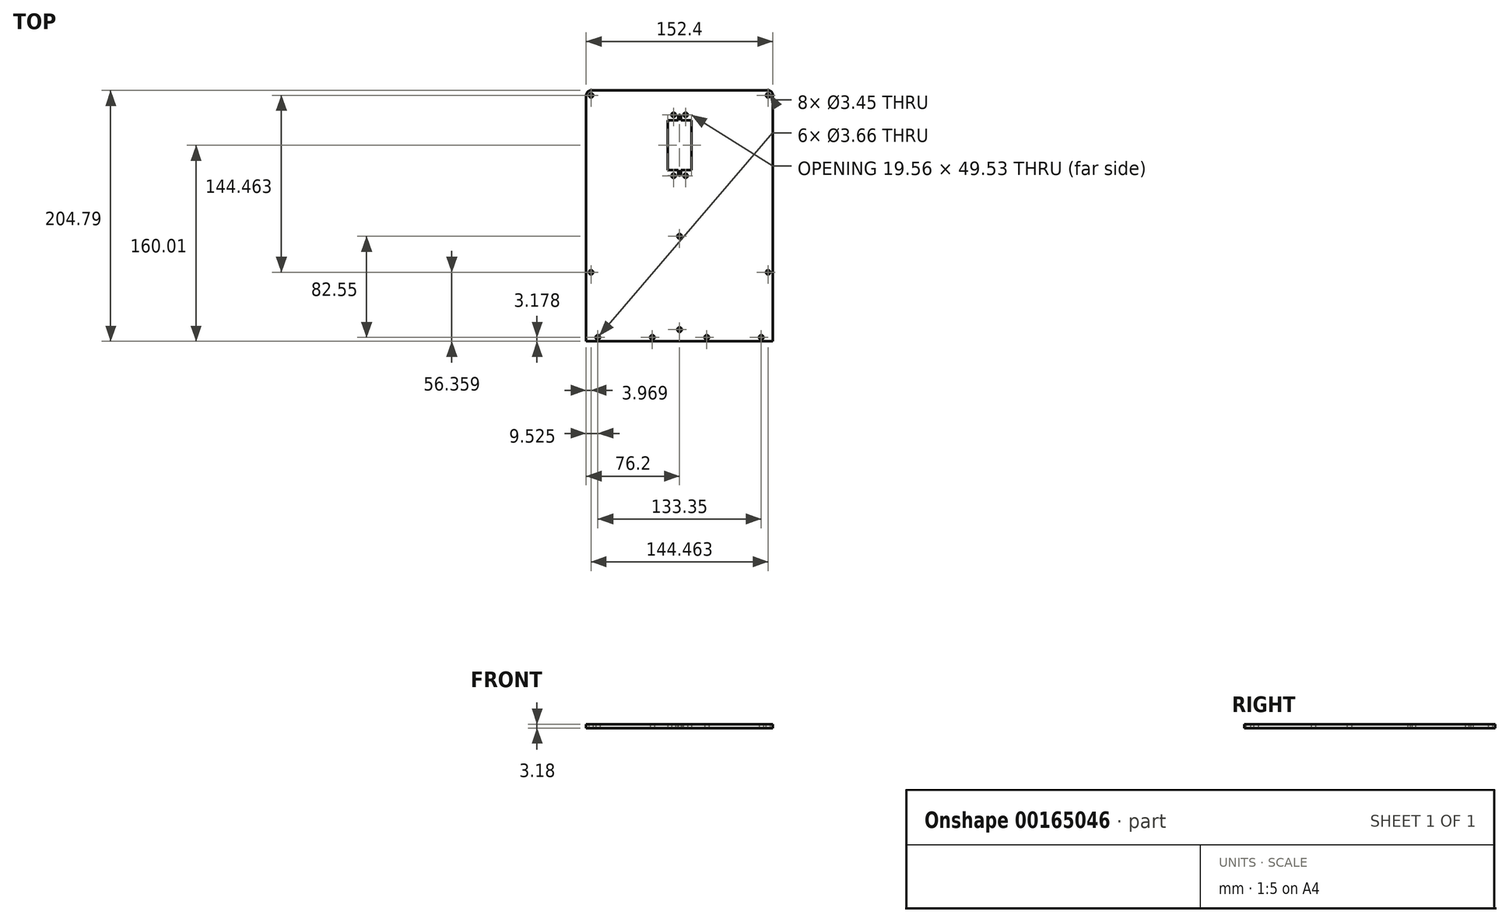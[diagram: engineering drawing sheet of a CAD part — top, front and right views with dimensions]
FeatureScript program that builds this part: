
annotation { "Feature Type Name" : "Feature", "Feature Type Description" : "" }
export const myFeature = defineFeature(function(context is Context, id is Id, definition is map)
    precondition{}
    {
        {
            var Q0;
            Q0=qCreatedBy(makeId("Top.planeOp"),FACE);
            var sketch = newSketch(context, id + "F0", { "sketchPlane" : qUnion([Q0])});
            skPoint(sketch, "E0.middle", {"position": v(0, 0) * mm});
            skLineSegment(sketch, "E1.bottom", {"start": v(-72.23, 72.23) * mm, "end": v(72.23, 72.23) * mm, "construction": true});
            skLineSegment(sketch, "E1.top", {"start": v(-72.23, -72.23) * mm, "end": v(72.23, -72.23) * mm, "construction": true});
            skLineSegment(sketch, "E1.left", {"start": v(-72.23, 72.23) * mm, "end": v(-72.23, -72.23) * mm, "construction": true});
            skLineSegment(sketch, "E1.right", {"start": v(72.23, 72.23) * mm, "end": v(72.23, -72.23) * mm, "construction": true});
            skCircle(sketch, "E2", {"center": v(-72.23, 72.23) * mm, "radius": 1.73 * mm});
            skCircle(sketch, "E3", {"center": v(72.23, 72.23) * mm, "radius": 1.73 * mm});
            skCircle(sketch, "E4", {"center": v(72.23, -72.23) * mm, "radius": 1.73 * mm});
            skCircle(sketch, "E5", {"center": v(-72.23, -72.23) * mm, "radius": 1.73 * mm});
            skLineSegment(sketch, "E6.bottom", {"start": v(76.2, -128.59) * mm, "end": v(-76.2, -128.59) * mm});
            skLineSegment(sketch, "E6.top", {"start": v(76.2, 76.2) * mm, "end": v(-76.2, 76.2) * mm});
            skLineSegment(sketch, "E6.left", {"start": v(76.2, -128.59) * mm, "end": v(76.2, 76.2) * mm});
            skLineSegment(sketch, "E6.right", {"start": v(-76.2, -128.59) * mm, "end": v(-76.2, 76.2) * mm});
            skLineSegment(sketch, "E7", {"start": v(0, 72.23) * mm, "end": v(0, 76.2) * mm, "construction": true});
            skLineSegment(sketch, "E8", {"start": v(-72.23, 72.23) * mm, "end": v(-76.2, 72.23) * mm, "construction": true});
            skLineSegment(sketch, "E9", {"start": v(66.68, -125.41) * mm, "end": v(76.2, -125.41) * mm, "construction": true});
            skCircle(sketch, "E10", {"center": v(-66.68, -125.41) * mm, "radius": 1.83 * mm});
            skCircle(sketch, "E11", {"center": v(22.23, -125.41) * mm, "radius": 1.83 * mm});
            skCircle(sketch, "E12", {"center": v(66.68, -125.41) * mm, "radius": 1.83 * mm});
            skLineSegment(sketch, "E13", {"start": v(22.23, -125.41) * mm, "end": v(66.68, -125.41) * mm, "construction": true});
            skLineSegment(sketch, "E14", {"start": v(22.23, -125.41) * mm, "end": v(-22.23, -125.41) * mm, "construction": true});
            skLineSegment(sketch, "E15", {"start": v(-22.23, -125.41) * mm, "end": v(-66.68, -125.41) * mm, "construction": true});
            skLineSegment(sketch, "E16", {"start": v(0, -125.41) * mm, "end": v(0, -128.59) * mm, "construction": true});
            skCircle(sketch, "E17", {"center": v(-22.23, -125.41) * mm, "radius": 1.83 * mm});
            skLineSegment(sketch, "E18", {"start": v(0, 0) * mm, "end": v(0, -42.86) * mm, "construction": true});
            skLineSegment(sketch, "E19", {"start": v(0, -42.86) * mm, "end": v(0, -119.06) * mm, "construction": true});
            skLineSegment(sketch, "E20", {"start": v(0, -119.06) * mm, "end": v(0, -125.41) * mm, "construction": true});
            skCircle(sketch, "E21", {"center": v(0, -42.86) * mm, "radius": 1.83 * mm});
            skCircle(sketch, "E22", {"center": v(0, -119.06) * mm, "radius": 1.83 * mm});
            skLineSegment(sketch, "E23", {"start": v(0, 0) * mm, "end": v(0, 31.42) * mm, "construction": true});
            skLineSegment(sketch, "E24.bottom", {"start": v(4.89, 6.53) * mm, "end": v(-4.89, 6.53) * mm, "construction": true});
            skLineSegment(sketch, "E24.top", {"start": v(4.89, 56.31) * mm, "end": v(-4.89, 56.31) * mm, "construction": true});
            skLineSegment(sketch, "E24.left", {"start": v(4.89, 6.53) * mm, "end": v(4.89, 56.31) * mm, "construction": true});
            skLineSegment(sketch, "E24.right", {"start": v(-4.89, 6.53) * mm, "end": v(-4.89, 56.31) * mm, "construction": true});
            skPoint(sketch, "E24.middle", {"position": v(0, 31.42) * mm});
            skCircle(sketch, "E25", {"center": v(4.89, 56.31) * mm, "radius": 3.97 * mm, "construction": true});
            skLineSegment(sketch, "E26", {"start": v(9.78, 31.42) * mm, "end": v(-9.78, 31.42) * mm, "construction": true});
            skLineSegment(sketch, "E27.bottom", {"start": v(1.02, 51.74) * mm, "end": v(9.78, 51.74) * mm});
            skLineSegment(sketch, "E27.top", {"start": v(1.02, 11.1) * mm, "end": v(9.78, 11.1) * mm});
            skLineSegment(sketch, "E27.right", {"start": v(9.78, 51.74) * mm, "end": v(9.78, 11.1) * mm});
            skLineSegment(sketch, "E28.bottom", {"start": v(-9.78, 51.74) * mm, "end": v(-1.02, 51.74) * mm});
            skLineSegment(sketch, "E28.top", {"start": v(-9.78, 11.1) * mm, "end": v(-1.02, 11.1) * mm});
            skLineSegment(sketch, "E28.left", {"start": v(-9.78, 51.74) * mm, "end": v(-9.78, 11.1) * mm});
            skLineSegment(sketch, "E29.bottom", {"start": v(1.02, 11.1) * mm, "end": v(-1.02, 11.1) * mm, "construction": true});
            skLineSegment(sketch, "E29.top", {"start": v(1.02, 7.67) * mm, "end": v(-1.02, 7.67) * mm, "construction": true});
            skLineSegment(sketch, "E29.left", {"start": v(1.02, 11.1) * mm, "end": v(1.02, 7.67) * mm});
            skLineSegment(sketch, "E29.right", {"start": v(-1.02, 11.1) * mm, "end": v(-1.02, 7.67) * mm});
            skLineSegment(sketch, "E30.bottom", {"start": v(-1.02, 51.74) * mm, "end": v(1.02, 51.74) * mm, "construction": true});
            skLineSegment(sketch, "E30.top", {"start": v(-1.02, 55.17) * mm, "end": v(1.02, 55.17) * mm, "construction": true});
            skLineSegment(sketch, "E30.left", {"start": v(-1.02, 51.74) * mm, "end": v(-1.02, 55.17) * mm});
            skLineSegment(sketch, "E30.right", {"start": v(1.02, 51.74) * mm, "end": v(1.02, 55.17) * mm});
            skArc(sketch, "E31", {"start": v(-1.02, 7.67) * mm, "mid": v(0, 6.66) * mm, "end": v(1.02, 7.67) * mm});
            skArc(sketch, "E32", {"start": v(1.02, 55.17) * mm, "mid": v(0, 56.19) * mm, "end": v(-1.02, 55.17) * mm});
            skCircle(sketch, "E33", {"center": v(4.89, 6.53) * mm, "radius": 1.73 * mm});
            skCircle(sketch, "E34", {"center": v(-4.89, 6.53) * mm, "radius": 1.73 * mm});
            skCircle(sketch, "E35", {"center": v(-4.89, 56.31) * mm, "radius": 1.73 * mm});
            skCircle(sketch, "E36", {"center": v(4.89, 56.31) * mm, "radius": 1.73 * mm});
            skCircle(sketch, "E37", {"center": v(0, 0) * mm, "radius": 63.48 * mm, "construction": true});
            skLineSegment(sketch, "E38", {"start": v(0, 51.74) * mm, "end": v(0, 42.32) * mm, "construction": true});
            skCircle(sketch, "E39", {"center": v(0, 42.32) * mm, "radius": 21.16 * mm, "construction": true});
            skSolve(sketch);
        }
        {
            var Q0;
            Q0=qSketchRegion(id+"F0",true);
            extrude(context, id + "F1", {"entities" : qUnion([Q0]), "depth" : 3.17 * mm});
        }
        {
            var Q0;
            Q0=makeQuery(id+"F1.opExtrude","SWEPT_EDGE",EDGE,{"disambiguationData":[OSD([sQuery(id+"F0.wireOp",EDGE,"E6.top"),sQuery(id+"F0.wireOp",EDGE,"E6.right")])]});
            var Q1;
            Q1=makeQuery(id+"F1.opExtrude","SWEPT_EDGE",EDGE,{"disambiguationData":[OSD([sQuery(id+"F0.wireOp",EDGE,"E6.top"),sQuery(id+"F0.wireOp",EDGE,"E6.left")])]});
            fillet(context, id + "F2", {"entities" : qUnion([Q0, Q1]), "radius" : 3.97 * mm, "tangentPropagation" : true, "allowEdgeOverflow" : false});
        }
    });
